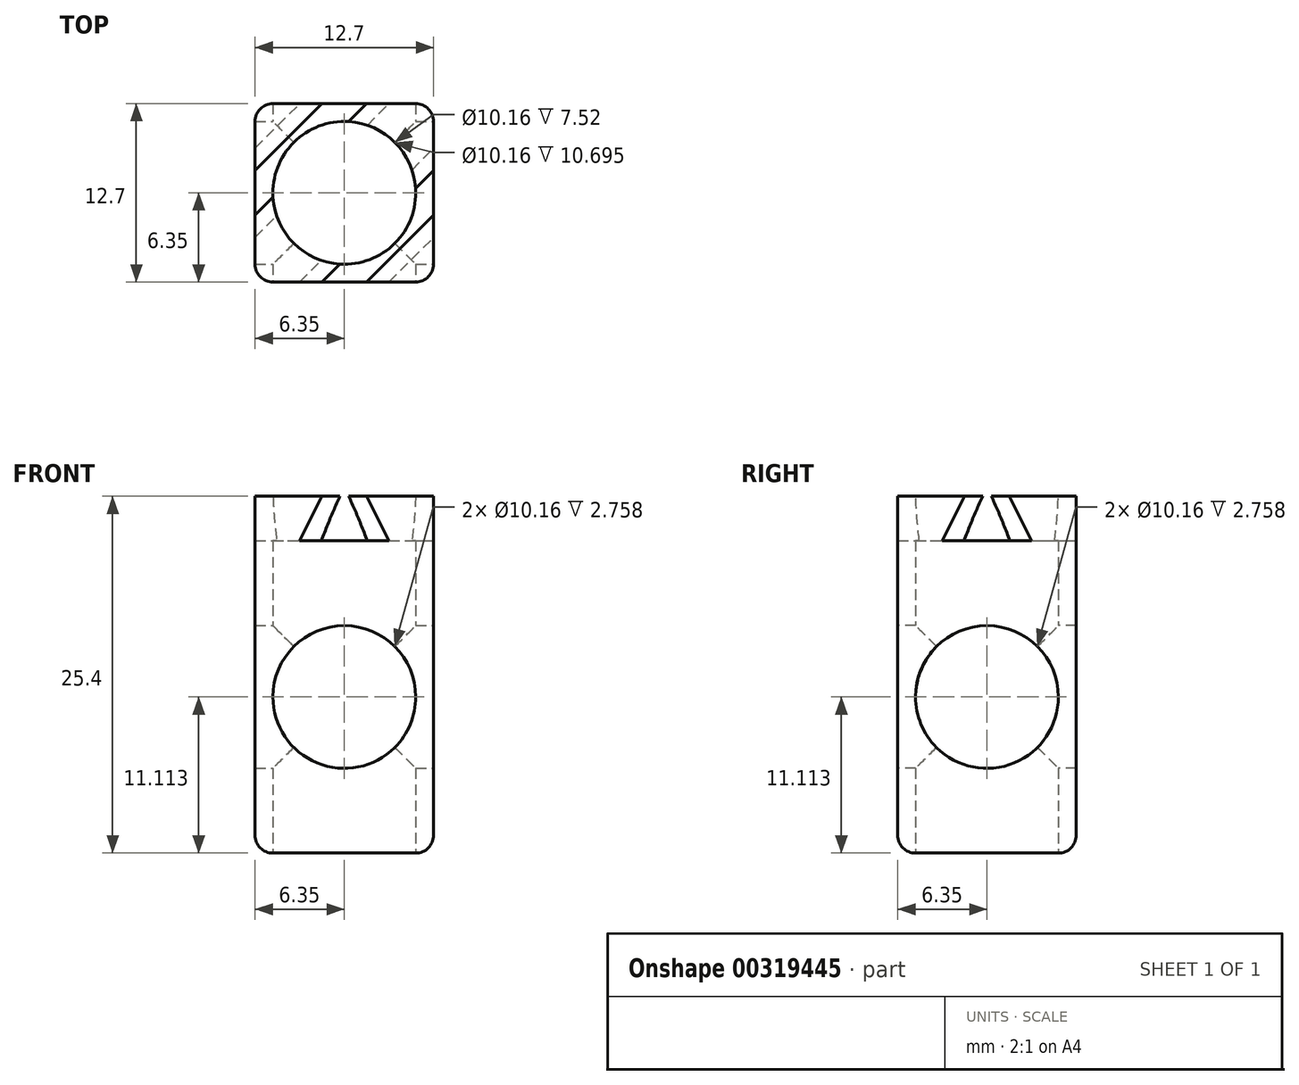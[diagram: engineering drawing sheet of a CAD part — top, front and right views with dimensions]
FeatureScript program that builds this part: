
annotation { "Feature Type Name" : "Feature", "Feature Type Description" : "" }
export const myFeature = defineFeature(function(context is Context, id is Id, definition is map)
    precondition{}
    {
        {
            var Q0;
            Q0=qCreatedBy(makeId("Top.planeOp"),FACE);
            var sketch = newSketch(context, id + "F0", { "sketchPlane" : qUnion([Q0])});
            skLineSegment(sketch, "E0.bottom", {"start": v(-6.35, 6.35) * mm, "end": v(6.35, 6.35) * mm});
            skLineSegment(sketch, "E0.top", {"start": v(-6.35, -6.35) * mm, "end": v(6.35, -6.35) * mm});
            skLineSegment(sketch, "E0.left", {"start": v(-6.35, 6.35) * mm, "end": v(-6.35, -6.35) * mm});
            skLineSegment(sketch, "E0.right", {"start": v(6.35, 6.35) * mm, "end": v(6.35, -6.35) * mm});
            skSolve(sketch);
        }
        {
            var Q0;
            Q0=makeQuery(id+"F0.imprint","IMPRINT",FACE,{"disambiguationData":[TD([[makeQuery(id+"F0.imprint","IMPRINT",EDGE,{"derivedFrom":sQuery(id+"F0.wireOp",EDGE,"E0.bottom")}),-1.0]])]});
            extrude(context, id + "F1", {"entities" : qUnion([Q0]), "depth" : 25.4 * mm});
        }
        {
            var Q0;
            Q0=makeQuery(id+"F1.opExtrude","SWEPT_FACE",FACE,{"disambiguationData":[OSD([sQuery(id+"F0.wireOp",EDGE,"E0.top")])]});
            var sketch = newSketch(context, id + "F2", { "sketchPlane" : qUnion([Q0])});
            skLineSegment(sketch, "E1", {"start": v(1.59, 25.4) * mm, "end": v(3.18, 22.23) * mm});
            skLineSegment(sketch, "E2", {"start": v(3.18, 22.23) * mm, "end": v(-3.17, 22.23) * mm});
            skLineSegment(sketch, "E3", {"start": v(-3.17, 22.23) * mm, "end": v(-1.59, 25.4) * mm});
            skLineSegment(sketch, "E4", {"start": v(-1.59, 25.4) * mm, "end": v(1.59, 25.4) * mm});
            skSolve(sketch);
        }
        {
            var Q0;
            Q0=makeQuery(id+"F1.opExtrude","SWEPT_FACE",FACE,{"disambiguationData":[OSD([sQuery(id+"F0.wireOp",EDGE,"E0.right")])]});
            var sketch = newSketch(context, id + "F3", { "sketchPlane" : qUnion([Q0])});
            skLineSegment(sketch, "E5", {"start": v(1.59, 25.4) * mm, "end": v(3.17, 22.23) * mm});
            skLineSegment(sketch, "E6", {"start": v(3.18, 22.23) * mm, "end": v(-3.17, 22.23) * mm});
            skLineSegment(sketch, "E7", {"start": v(-3.17, 22.23) * mm, "end": v(-1.59, 25.4) * mm});
            skLineSegment(sketch, "E8", {"start": v(-1.59, 25.4) * mm, "end": v(1.59, 25.4) * mm});
            skSolve(sketch);
        }
        {
            var Q1;
            Q1=makeQuery(id+"F2.imprint","IMPRINT",FACE,{"disambiguationData":[TD([[makeQuery(id+"F2.imprint","IMPRINT",EDGE,{"derivedFrom":sQuery(id+"F2.wireOp",EDGE,"E1")}),-1.0]])]});
            var Q2;
            Q2=makeQuery(id+"F3.imprint","IMPRINT",FACE,{"disambiguationData":[TD([[makeQuery(id+"F3.imprint","IMPRINT",EDGE,{"derivedFrom":sQuery(id+"F3.wireOp",EDGE,"E5")}),-1.0]])]});
            loft(context, id + "F4", {"operationType" : NewBodyOperationType.REMOVE, "sheetProfilesArray" : [{ "sheetProfileEntities" : qUnion([Q1]) }, { "sheetProfileEntities" : qUnion([Q2]) }]});
        }
        {
            var Q0;
            Q0=makeQuery(id+"F1.opExtrude","SWEPT_FACE",FACE,{"disambiguationData":[OSD([sQuery(id+"F0.wireOp",EDGE,"E0.bottom")])]});
            var sketch = newSketch(context, id + "F5", { "sketchPlane" : qUnion([Q0])});
            skLineSegment(sketch, "E9", {"start": v(1.59, 25.4) * mm, "end": v(3.18, 22.23) * mm});
            skLineSegment(sketch, "E10", {"start": v(3.18, 22.23) * mm, "end": v(-3.17, 22.23) * mm});
            skLineSegment(sketch, "E11", {"start": v(-3.17, 22.23) * mm, "end": v(-1.59, 25.4) * mm});
            skLineSegment(sketch, "E12", {"start": v(-1.59, 25.4) * mm, "end": v(1.59, 25.4) * mm});
            skSolve(sketch);
        }
        {
            var Q0;
            Q0=makeQuery(id+"F1.opExtrude","SWEPT_FACE",FACE,{"disambiguationData":[OSD([sQuery(id+"F0.wireOp",EDGE,"E0.left")])]});
            var sketch = newSketch(context, id + "F6", { "sketchPlane" : qUnion([Q0])});
            skLineSegment(sketch, "E13", {"start": v(1.59, 25.4) * mm, "end": v(3.18, 22.23) * mm});
            skLineSegment(sketch, "E14", {"start": v(3.18, 22.23) * mm, "end": v(-3.17, 22.23) * mm});
            skLineSegment(sketch, "E15", {"start": v(-3.17, 22.23) * mm, "end": v(-1.59, 25.4) * mm});
            skLineSegment(sketch, "E16", {"start": v(-1.59, 25.4) * mm, "end": v(1.59, 25.4) * mm});
            skSolve(sketch);
        }
        {
            var Q1;
            Q1=makeQuery(id+"F6.imprint","IMPRINT",FACE,{"disambiguationData":[TD([[makeQuery(id+"F6.imprint","IMPRINT",EDGE,{"derivedFrom":sQuery(id+"F6.wireOp",EDGE,"E13")}),-1.0]])]});
            var Q2;
            Q2=makeQuery(id+"F5.imprint","IMPRINT",FACE,{"disambiguationData":[TD([[makeQuery(id+"F5.imprint","IMPRINT",EDGE,{"derivedFrom":sQuery(id+"F5.wireOp",EDGE,"E9")}),-1.0]])]});
            loft(context, id + "F7", {"operationType" : NewBodyOperationType.REMOVE, "sheetProfilesArray" : [{ "sheetProfileEntities" : qUnion([Q1]) }, { "sheetProfileEntities" : qUnion([Q2]) }]});
        }
        {
            var Q0;
            Q0=makeQuery(id+"F1.opExtrude","CAP_FACE",FACE,{"disambiguationData":[OSD([sQuery(id+"F0.wireOp",EDGE,"E0.bottom"),sQuery(id+"F0.wireOp",EDGE,"E0.top"),sQuery(id+"F0.wireOp",EDGE,"E0.left"),sQuery(id+"F0.wireOp",EDGE,"E0.right")])],"isStart":true});
            var sketch = newSketch(context, id + "F8", { "sketchPlane" : qUnion([Q0])});
            skCircle(sketch, "E17", {"center": v(0, 0) * mm, "radius": 5.08 * mm});
            skSolve(sketch);
        }
        {
            var Q0;
            Q0=makeQuery(id+"F8.imprint","IMPRINT",FACE,{"disambiguationData":[TD([[makeQuery(id+"F8.imprint","IMPRINT",EDGE,{"derivedFrom":sQuery(id+"F8.wireOp",EDGE,"E17")}),1.0]])]});
            extrude(context, id + "F9", {"entities" : qUnion([Q0]), "operationType" : NewBodyOperationType.REMOVE, "oppositeDirection" : true, "depth" : 25.4 * mm});
        }
        {
            var Q0;
            Q0=makeQuery(id+"F1.opExtrude","SWEPT_FACE",FACE,{"disambiguationData":[OSD([sQuery(id+"F0.wireOp",EDGE,"E0.top")])]});
            var sketch = newSketch(context, id + "F10", { "sketchPlane" : qUnion([Q0])});
            skCircle(sketch, "E18", {"center": v(0, 11.11) * mm, "radius": 5.08 * mm});
            skPoint(sketch, "E18.centerSnap0", {"position": v(6.35, 12.7) * mm});
            skLineSegment(sketch, "E19", {"start": v(0, 22.23) * mm, "end": v(0, 11.11) * mm});
            skLineSegment(sketch, "E20", {"start": v(0, 11.11) * mm, "end": v(0, 0) * mm});
            skSolve(sketch);
        }
        {
            var Q0;
            {var subQ0=sQuery(id+"F10.wireOp",EDGE,"E19");var subQ1=sQuery(id+"F10.wireOp",EDGE,"E18");var subQ2=makeQuery(id+"F10.imprint","INTERSECT",VERTEX,{"derivedFrom":[subQ1,subQ0]});Q0=makeQuery(id+"F10.imprint","IMPRINT",FACE,{"disambiguationData":[TD([[makeQuery(id+"F10.imprint","IMPRINT",EDGE,{"disambiguationData":[TD([[subQ2,-1.0]])],"derivedFrom":subQ1}),1.0]])]});}
            var Q1;
            {var subQ0=sQuery(id+"F10.wireOp",EDGE,"E19");var subQ1=sQuery(id+"F10.wireOp",EDGE,"E18");var subQ2=makeQuery(id+"F10.imprint","INTERSECT",VERTEX,{"derivedFrom":[subQ1,subQ0]});Q1=makeQuery(id+"F10.imprint","IMPRINT",FACE,{"disambiguationData":[TD([[makeQuery(id+"F10.imprint","IMPRINT",EDGE,{"disambiguationData":[TD([[subQ2,1.0]])],"derivedFrom":subQ1}),1.0]])]});}
            extrude(context, id + "F11", {"entities" : qUnion([Q0, Q1]), "oppositeDirection" : true, "depth" : 25.4 * mm});
        }
        {
            var Q0;
            Q0=makeQuery(id+"F11.opExtrude","SWEPT_BODY",BODY,{"disambiguationData":[OSD([sQuery(id+"F10.wireOp",EDGE,"E18")])]});
            var Q1;
            Q1=makeQuery(id+"F1.opExtrude","SWEPT_EDGE",EDGE,{"disambiguationData":[OSD([sQuery(id+"F0.wireOp",EDGE,"E0.bottom"),sQuery(id+"F0.wireOp",EDGE,"E0.right")])]});
            circularPattern(context, id + "F12", {"operationType" : NewBodyOperationType.REMOVE, "entities" : qUnion([Q0]), "axis" : qUnion([Q1]), "angle" : 360 * degree, "instanceCount" : 4, "equalSpace" : true});
        }
        {
            var Q0;
            Q0=makeQuery(id+"F1.opExtrude","CAP_EDGE",EDGE,{"disambiguationData":[OSD([sQuery(id+"F0.wireOp",EDGE,"E0.top")])],"isStart":true});
            var Q1;
            Q1=makeQuery(id+"F1.opExtrude","SWEPT_EDGE",EDGE,{"disambiguationData":[OSD([sQuery(id+"F0.wireOp",EDGE,"E0.top"),sQuery(id+"F0.wireOp",EDGE,"E0.right")])]});
            var Q2;
            Q2=makeQuery(id+"F1.opExtrude","SWEPT_EDGE",EDGE,{"disambiguationData":[OSD([sQuery(id+"F0.wireOp",EDGE,"E0.bottom"),sQuery(id+"F0.wireOp",EDGE,"E0.right")])]});
            var Q3;
            Q3=makeQuery(id+"F1.opExtrude","CAP_EDGE",EDGE,{"disambiguationData":[OSD([sQuery(id+"F0.wireOp",EDGE,"E0.right")])],"isStart":true});
            var Q4;
            Q4=makeQuery(id+"F1.opExtrude","SWEPT_EDGE",EDGE,{"disambiguationData":[OSD([sQuery(id+"F0.wireOp",EDGE,"E0.bottom"),sQuery(id+"F0.wireOp",EDGE,"E0.left")])]});
            var Q5;
            Q5=makeQuery(id+"F1.opExtrude","CAP_EDGE",EDGE,{"disambiguationData":[OSD([sQuery(id+"F0.wireOp",EDGE,"E0.bottom")])],"isStart":true});
            var Q6;
            Q6=makeQuery(id+"F1.opExtrude","CAP_EDGE",EDGE,{"disambiguationData":[OSD([sQuery(id+"F0.wireOp",EDGE,"E0.left")])],"isStart":true});
            var Q7;
            Q7=makeQuery(id+"F1.opExtrude","SWEPT_EDGE",EDGE,{"disambiguationData":[OSD([sQuery(id+"F0.wireOp",EDGE,"E0.top"),sQuery(id+"F0.wireOp",EDGE,"E0.left")])]});
            fillet(context, id + "F13", {"entities" : qUnion([Q0, Q1, Q2, Q3, Q4, Q5, Q6, Q7]), "radius" : 1.27 * mm, "tangentPropagation" : true, "allowEdgeOverflow" : false});
        }
    });
